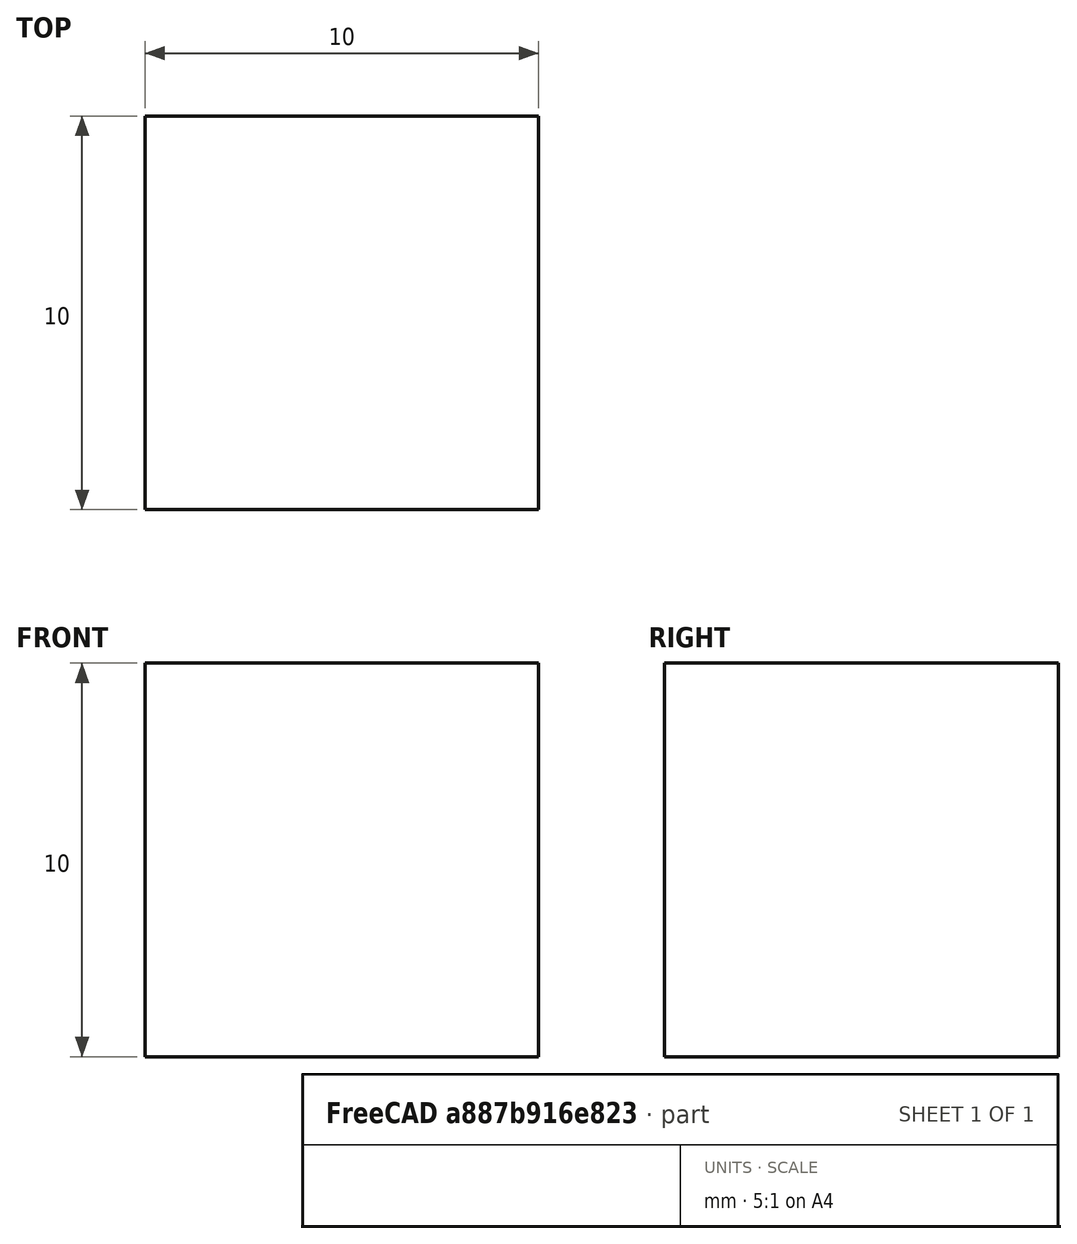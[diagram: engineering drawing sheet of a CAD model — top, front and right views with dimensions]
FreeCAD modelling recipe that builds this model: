
FCSTD DOCUMENT  (FreeCAD 0.21R33694 (Git))
Label: Simple Shear
License: All rights reserved
LicenseURL: http://en.wikipedia.org/wiki/All_rights_reserved
objects: Fem::ConstraintForce×4, Fem::FemMeshObjectPython×2, Fem::ConstraintDisplacement×2, Part::Box×1, Fem::FemSolverObjectPython×1, App::MaterialObjectPython×1, Fem::ConstraintFixed×1, Fem::FemResultObjectPython×1, Fem::FemAnalysis×1
note: 1 computed .brp shape members not serialized (recipe doc carries the construction recipe); baked Part::Feature solids carry a one-line shape summary decoded from their .brp

FEATURE [Part::Box] Box  label="Cube"
  AttacherType = Attacher::AttachEngine3D
  Height = 10
  Length = 10
  Width = 10
FEATURE [Fem::FemSolverObjectPython] SolverCcxTools  # FEM object (typed FeaturePython)
  AnalysisType = 0
  BeamShellResultOutput3D = false
  BucklingFactors = 1
  EigenmodeHighLimit = 1000000
  EigenmodeLowLimit = 0
  EigenmodesCount = 10
  GeometricalNonlinearity = 0
  IterationsControlParameterCutb = 0.25,0.5,0.75,0.85,,,1.5,
  IterationsControlParameterIter = 4,8,9,200,10,400,,200,,
  IterationsControlParameterTimeUse = false
  IterationsThermoMechMaximum = 2000
  IterationsUserDefinedIncrementations = false
  IterationsUserDefinedTimeStepLength = false
  MaterialNonlinearity = 0
  MatrixSolverType = 0
  SplitInputWriter = false
  ThermoMechSteadyState = true
  TimeEnd = 1
  TimeInitialStep = 0.01
FEATURE [App::MaterialObjectPython] MaterialSolid  # material (typed FeaturePython)
  Category = 0
  Material = AuthorAndLicense=(c) 2013 Yorik van Havre (CC-BY 3.0),CardName=Concrete-Generic,CompressiveStrength=25 MPa,Density=2400 kg/m^3,+7 more (map truncated)
FEATURE [Fem::FemMeshObjectPython] FEMMeshGmsh  # FEM object (typed FeaturePython)
  Algorithm2D = 0
  Algorithm3D = 0
  CharacteristicLengthMax = 0
  CharacteristicLengthMin = 10
  CoherenceMesh = true
  ElementDimension = 0
  ElementOrder = 1
  GeometryTolerance = 1e-06
  GroupsOfNodes = false
  HighOrderOptimize = 0
  MeshSizeFromCurvature = 12
  OptimizeNetgen = false
  OptimizeStd = true
  Part = -> Box
  RecombinationAlgorithm = 0
  Recombine3DAll = false
  RecombineAll = false
  SecondOrderLinear = false
FEATURE [Fem::ConstraintForce] ConstraintForce
  Direction = -> Box [Edge10]
  DirectionVector = (1,0,0)
  Force = 10000
  NormalDirection = (0,0,1)
  Points = (9) [(0,0,10),(5,0,10),(10,0,10),(0,5,10),(5,5,10),(10,5,10),(0,10,10),(5,10,10),(10,10,10)]
  References = -> [Box]
FEATURE [Fem::ConstraintForce] ConstraintForce001
  Direction = -> Box [Edge5]
  DirectionVector = (0,0,1)
  Force = 10000
  NormalDirection = (1,0,0)
  Points = (9) [(10,10,0),(10,10,5),(10,10,10),(10,5,0),(10,5,5),(10,5,10),(10,0,0),(10,0,5),(10,0,10)]
  References = -> [Box]
FEATURE [Fem::ConstraintForce] ConstraintForce002
  Direction = -> Box [Edge1]
  DirectionVector = (0,0,-1)
  Force = 10000
  NormalDirection = (-1,0,0)
  Points = (9) [(0,10,0),(0,10,5),(0,10,10),(0,5,0),(0,5,5),(0,5,10),(0,0,0),(0,0,5),(0,0,10)]
  References = -> [Box]
  Reversed = true
FEATURE [Fem::ConstraintForce] ConstraintForce003
  Direction = -> Box [Edge9]
  DirectionVector = (-1,0,0)
  Force = 10000
  NormalDirection = (0,0,-1)
  Points = (9) [(0,0,0),(5,0,0),(10,0,0),(0,5,0),(5,5,0),(10,5,0),(0,10,0),(5,10,0),(10,10,0)]
  References = -> [Box]
  Reversed = true
FEATURE [Fem::ConstraintFixed] ConstraintFixed
  NormalDirection = (0,0,1)
  Normals = (1) [(0,0,1)]
  Points = (1) [(0,0,0)]
  References = -> [Box]
  Scale = 2
FEATURE [Fem::ConstraintDisplacement] ConstraintDisplacement
  NormalDirection = (0,0,1)
  Normals = (1) [(0,0,1)]
  Points = (1) [(0,10,0)]
  References = -> [Box]
  Scale = 2
  hasXFormula = false
  hasYFormula = false
  hasZFormula = false
  rotxFix = false
  rotxFree = true
  rotyFix = false
  rotyFree = true
  rotzFix = false
  rotzFree = true
  useFlowSurfaceForce = false
  xDisplacement = 0
  xFix = false
  xFree = false
  xRotation = 0
  yDisplacement = 0
  yFix = false
  yFree = true
  yRotation = 0
  zDisplacement = 0
  zFix = false
  zFree = false
  zRotation = 0
FEATURE [Fem::ConstraintDisplacement] ConstraintDisplacement001
  NormalDirection = (0,0,1)
  Normals = (1) [(0,0,1)]
  Points = (1) [(10,0,0)]
  References = -> [Box]
  Scale = 2
  hasXFormula = false
  hasYFormula = false
  hasZFormula = false
  rotxFix = false
  rotxFree = true
  rotyFix = false
  rotyFree = true
  rotzFix = false
  rotzFree = true
  useFlowSurfaceForce = false
  xDisplacement = 0
  xFix = false
  xFree = true
  xRotation = 0
  yDisplacement = 0
  yFix = false
  yFree = true
  yRotation = 0
  zDisplacement = 0
  zFix = false
  zFree = false
  zRotation = 0
FEATURE [Fem::FemMeshObjectPython] Result_Mesh_Volume  # FEM object (typed FeaturePython)
FEATURE [Fem::FemResultObjectPython] ResultMechanical  # FEM object (typed FeaturePython)
  CriticalStrainRatio = [0,0,0,0,0,0,0,0,0,0,0,0,0,0,0,0,0,0,0,0,0,0,0,0,0,0,0,0,0,0,0,0,0,0,0,0,0,0,0,0,0,0,0,0,0,0,0,0,0,0,0,0,0,0,0,0,0,0,0,0,0,0,0]
  DisplacementLengths = [0.000672145,0,0.000672145,8.08776e-19,0.000695916,2.37856e-05,0.000695916,2.37856e-05,0.000336072,0.000672145,0.000336072,8.58475e-19,0.000359844,0.000695916,0.000359844,2.37856e-05,1.18928e-05,0.00068403,1.18928e-05,0.00068403,0.000336072,+42 more]
  DisplacementVectors = (63) [(0.000671724,-3.07403e-18,2.37856e-05),(0,0,0),(0.000671724,-3.22728e-18,2.37856e-05),(0,-8.08776e-19,0),(0.00069551,-4.7067e-20,2.37856e-05),+58 more]
  Eigenmode = 0
  EigenmodeFrequency = 0
  Mesh = -> Result_Mesh_Volume
  NodeNumbers = [1,2,3,4,5,6,7,8,9,10,11,12,13,14,15,16,17,18,19,20,21,22,23,24,25,26,27,28,29,30,31,32,33,34,35,36,37,38,39,40,41,42,43,44,45,46,47,48,49,50,51,52,53,54,55,56,57,58,59,60,61,62,63]
  NodeStressXX = [0.000176,0.000176,0.000176,0.000176,0.000176,0.000176,0.000176,0.000176,0.000176,0.000176,0.000176,0.000176,0.000176,0.000176,0.000176,0.000176,0.000176,0.000176,0.000176,0.000176,0.000176,0.000176,0.000176,0.000176,0.000176,0.000176,+37 more]
  NodeStressXY = [-1.56796e-16,-1.95995e-17,1.76396e-16,-2.74394e-16,-1.08468e-30,3.13593e-16,-1.76396e-16,-2.35195e-16,-8.8198e-17,9.79977e-18,-4.89989e-17,-1.46997e-16,1.56796e-16,-8.8198e-17,-2.05795e-16,3.91991e-17,1.46997e-16,-7.83982e-17,-2.54794e-16,+44 more]
  NodeStressXZ = [0.499322,0.499322,0.499322,0.499322,0.499322,0.499322,0.499322,0.499322,0.499322,0.499322,0.499322,0.499322,0.499322,0.499322,0.499322,0.499322,0.499322,0.499322,0.499322,0.499322,0.499322,0.499322,0.499322,0.499322,0.499322,0.499322,+37 more]
  NodeStressYY = [-3.61341e-16,-1.20419e-15,-3.70757e-16,-1.10266e-15,-6.30839e-16,-4.02405e-16,-5.26641e-16,-5.25852e-16,-7.82768e-16,-3.66049e-16,-7.36708e-16,-1.15343e-15,-5.16622e-16,-5.7874e-16,-5.26246e-16,-4.64128e-16,-8.033e-16,-4.9609e-16,+45 more]
  NodeStressYZ = [1.56796e-16,1.95995e-17,-1.76396e-16,2.74394e-16,-8.75143e-31,-3.13593e-16,1.76396e-16,2.35195e-16,8.8198e-17,-9.79977e-18,4.89989e-17,1.46997e-16,-1.56796e-16,8.8198e-17,2.05795e-16,-3.91991e-17,-1.46997e-16,7.83982e-17,2.54794e-16,+44 more]
  NodeStressZZ = [0.000176,0.000176,0.000176,0.000176,0.000176,0.000176,0.000176,0.000176,0.000176,0.000176,0.000176,0.000176,0.000176,0.000176,0.000176,0.000176,0.000176,0.000176,0.000176,0.000176,0.000176,0.000176,0.000176,0.000176,0.000176,0.000176,+37 more]
  Peeq = [0,0,0,0,0,0,0,0,0,0,0,0,0,0,0,0,0,0,0,0,0,0,0,0,0,0,0,0,0,0,0,0,0,0,0,0,0,0,0,0,0,0,0,0,0,0,0,0,0,0,0,0,0,0,0,0,0,0,0,0,0,0,0]
  ResultType = Fem::ResultMechanical
  Stats = [-4.4267e-19,0.00069551,-3.22728e-18,3.14343e-18,-5.93401e-19,2.37856e-05,0,0.000695916,0,0,0,0,0,0,0,0,0,0,0,0,0,0,0,0,0,0]
  Temperature = [0,0,0,0,0,0,0,0,0,0,0,0,0,0,0,0,0,0,0,0,0,0,0,0,0,0,0,0,0,0,0,0,0,0,0,0,0,0,0,0,0,0,0,0,0,0,0,0,0,0,0,0,0,0,0,0,0,0,0,0,0,0,0]
  Time = 0
  vonMises = [0,0,0,0,0,0,0,0,0,0,0,0,0,0,0,0,0,0,0,0,0,0,0,0,0,0,0,0,0,0,0,0,0,0,0,0,0,0,0,0,0,0,0,0,0,0,0,0,0,0,0,0,0,0,0,0,0,0,0,0,0,0,0]
FEATURE [Fem::FemAnalysis] Analysis
  Group = -> [SolverCcxTools,MaterialSolid,FEMMeshGmsh,ConstraintForce,ConstraintForce001,ConstraintForce002,ConstraintForce003,ConstraintFixed,ConstraintDisplacement,ConstraintDisplacement001,ResultMechanical]
